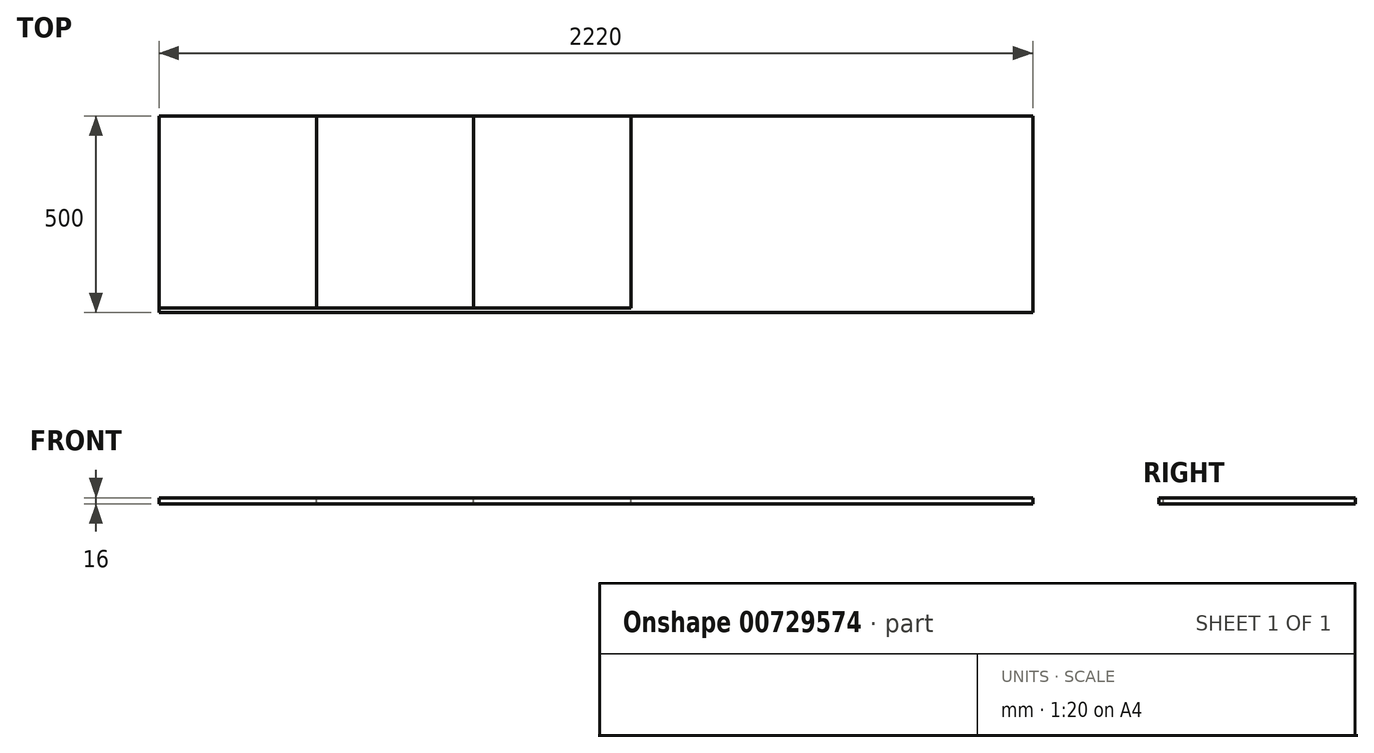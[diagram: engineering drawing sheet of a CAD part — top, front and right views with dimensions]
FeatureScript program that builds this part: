
annotation { "Feature Type Name" : "Feature", "Feature Type Description" : "" }
export const myFeature = defineFeature(function(context is Context, id is Id, definition is map)
    precondition{}
    {
        {
            var Q0;
            Q0=qCreatedBy(makeId("Top.planeOp"),FACE);
            var sketch = newSketch(context, id + "F0", { "sketchPlane" : qUnion([Q0])});
            skLineSegment(sketch, "E0.bottom", {"start": v(1110, -250) * mm, "end": v(-1110, -250) * mm});
            skLineSegment(sketch, "E0.top", {"start": v(1110, 250) * mm, "end": v(-1110, 250) * mm});
            skLineSegment(sketch, "E0.left", {"start": v(1110, -250) * mm, "end": v(1110, 250) * mm});
            skLineSegment(sketch, "E0.right", {"start": v(-1110, -250) * mm, "end": v(-1110, 250) * mm});
            skPoint(sketch, "E0.middle", {"position": v(0, 0) * mm});
            skSolve(sketch);
        }
        {
            var Q0;
            Q0=makeQuery(id+"F0.imprint","IMPRINT",FACE,{"disambiguationData":[TD([[makeQuery(id+"F0.imprint","IMPRINT",EDGE,{"derivedFrom":sQuery(id+"F0.wireOp",EDGE,"E0.bottom")}),-1.0]])]});
            extrude(context, id + "F1", {"entities" : qUnion([Q0]), "depth" : 16 * mm, "offsetDistance" : 25 * mm});
        }
        {
            var Q0;
            Q0=makeQuery(id+"F1.opExtrude","CAP_FACE",FACE,{"disambiguationData":[OSD([sQuery(id+"F0.wireOp",EDGE,"E0.bottom"),sQuery(id+"F0.wireOp",EDGE,"E0.top"),sQuery(id+"F0.wireOp",EDGE,"E0.left"),sQuery(id+"F0.wireOp",EDGE,"E0.right")])],"isStart":false});
            var sketch = newSketch(context, id + "F2", { "sketchPlane" : qUnion([Q0])});
            skLineSegment(sketch, "E1.bottom", {"start": v(-1110, 250) * mm, "end": v(-710, 250) * mm});
            skLineSegment(sketch, "E1.top", {"start": v(-1110, -238) * mm, "end": v(-710, -238) * mm});
            skLineSegment(sketch, "E1.left", {"start": v(-1110, 250) * mm, "end": v(-1110, -238) * mm});
            skLineSegment(sketch, "E1.right", {"start": v(-710, 250) * mm, "end": v(-710, -238) * mm});
            skLineSegment(sketch, "E2.bottom", {"start": v(-710, 250) * mm, "end": v(-310, 250) * mm});
            skLineSegment(sketch, "E2.top", {"start": v(-710, -238) * mm, "end": v(-310, -238) * mm});
            skLineSegment(sketch, "E2.right", {"start": v(-310, 250) * mm, "end": v(-310, -238) * mm});
            skLineSegment(sketch, "E3.bottom", {"start": v(-310, 250) * mm, "end": v(90, 250) * mm});
            skLineSegment(sketch, "E3.top", {"start": v(-310, -238) * mm, "end": v(90, -238) * mm});
            skLineSegment(sketch, "E3.right", {"start": v(90, 250) * mm, "end": v(90, -238) * mm});
            skSolve(sketch);
        }
        {
            var Q0;
            Q0=makeQuery(id+"F2.imprint","IMPRINT",FACE,{"disambiguationData":[TD([[makeQuery(id+"F2.imprint","IMPRINT",EDGE,{"derivedFrom":sQuery(id+"F2.wireOp",EDGE,"E1.bottom")}),1.0]])]});
            extrude(context, id + "F3", {"entities" : qUnion([Q0]), "oppositeDirection" : true, "depth" : 16 * mm, "offsetDistance" : 25 * mm});
        }
        {
            var Q0;
            Q0=makeQuery(id+"F2.imprint","IMPRINT",FACE,{"disambiguationData":[TD([[makeQuery(id+"F2.imprint","IMPRINT",EDGE,{"derivedFrom":sQuery(id+"F2.wireOp",EDGE,"E2.bottom")}),1.0]])]});
            extrude(context, id + "F4", {"entities" : qUnion([Q0]), "oppositeDirection" : true, "depth" : 16 * mm, "offsetDistance" : 25 * mm});
        }
        {
            var Q0;
            Q0=makeQuery(id+"F2.imprint","IMPRINT",FACE,{"disambiguationData":[TD([[makeQuery(id+"F2.imprint","IMPRINT",EDGE,{"derivedFrom":sQuery(id+"F2.wireOp",EDGE,"E3.bottom")}),1.0]])]});
            extrude(context, id + "F5", {"entities" : qUnion([Q0]), "oppositeDirection" : true, "depth" : 16 * mm, "offsetDistance" : 25 * mm});
        }
    });
